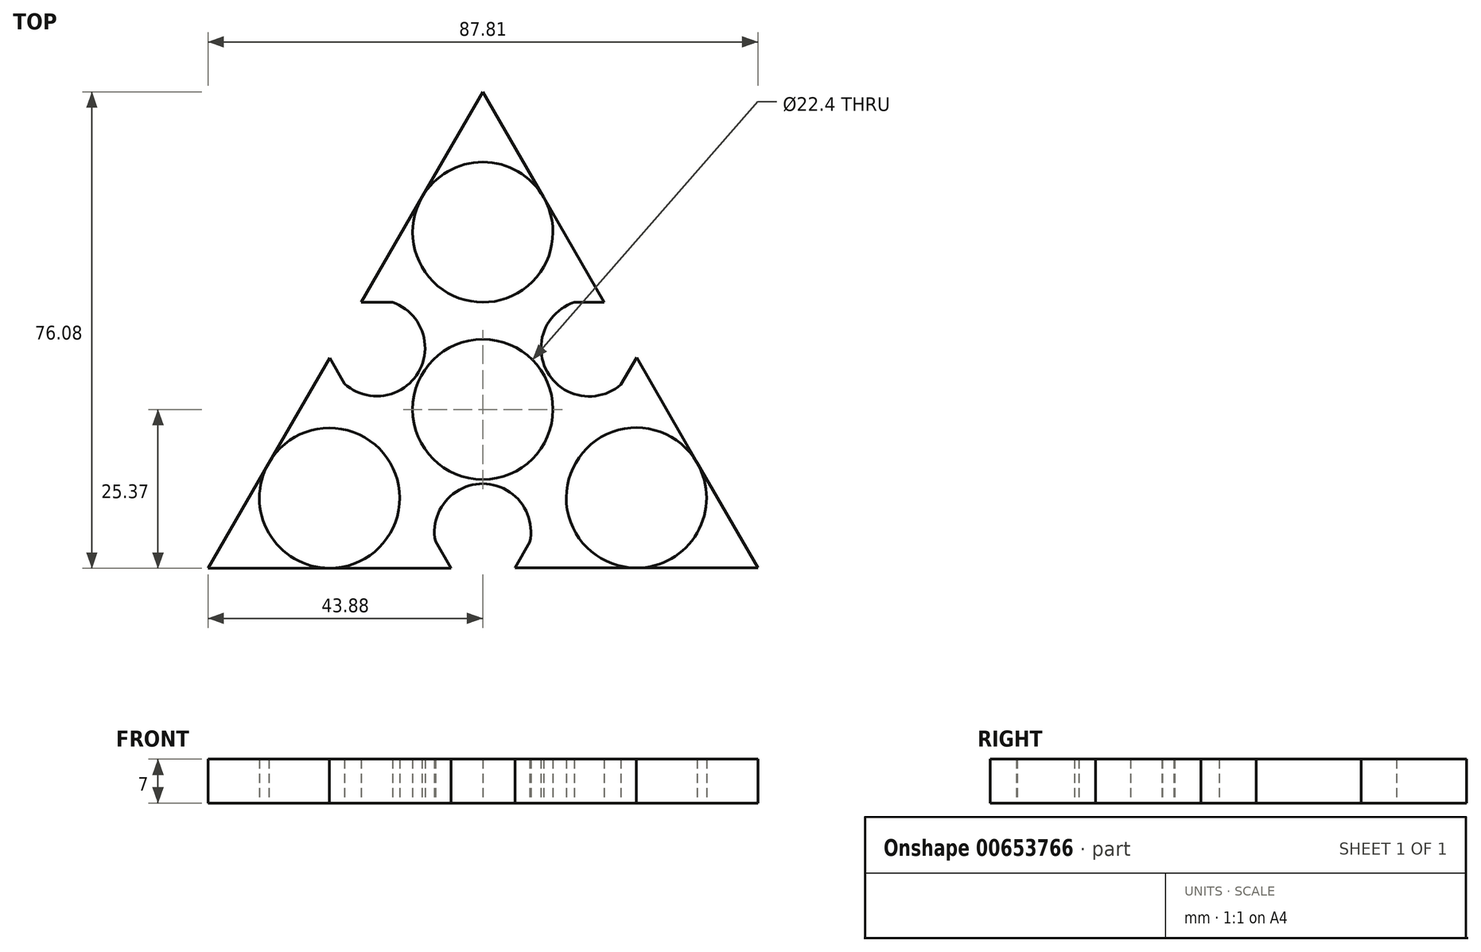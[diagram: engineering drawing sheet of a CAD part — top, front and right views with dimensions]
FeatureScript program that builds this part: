
annotation { "Feature Type Name" : "Feature", "Feature Type Description" : "" }
export const myFeature = defineFeature(function(context is Context, id is Id, definition is map)
    precondition{}
    {
        {
            var Q0;
            Q0=qCreatedBy(makeId("Top.planeOp"),FACE);
            var sketch = newSketch(context, id + "F0", { "sketchPlane" : qUnion([Q0])});
            skCircle(sketch, "E0", {"center": v(0, 0) * mm, "radius": 11.2 * mm});
            skCircle(sketch, "E1.cCircle", {"center": v(0, 28.3) * mm, "radius": 11.2 * mm, "construction": true});
            skLineSegment(sketch, "E1.0", {"start": v(-19.4, 17.12) * mm, "end": v(0.02, 50.7) * mm});
            skLineSegment(sketch, "E1.1", {"start": v(0.02, 50.7) * mm, "end": v(19.4, 17.1) * mm});
            skLineSegment(sketch, "E1.2", {"start": v(19.4, 17.1) * mm, "end": v(-19.4, 17.12) * mm});
            skPoint(sketch, "E1.0.midPoint", {"position": v(-9.7, 33.92) * mm});
            skCircle(sketch, "E2", {"center": v(0, 28.3) * mm, "radius": 11.2 * mm});
            skLineSegment(sketch, "E3.1.0", {"start": v(-43.88, -25.34) * mm, "end": v(-24.46, 8.25) * mm});
            skLineSegment(sketch, "E3.1.1", {"start": v(-5.08, -25.37) * mm, "end": v(-43.88, -25.34) * mm});
            skCircle(sketch, "E3.1.2", {"center": v(-24.47, -14.15) * mm, "radius": 11.2 * mm, "construction": true});
            skLineSegment(sketch, "E3.1.3", {"start": v(-24.46, 8.25) * mm, "end": v(-5.08, -25.37) * mm});
            skLineSegment(sketch, "E3.2.0", {"start": v(43.93, -25.33) * mm, "end": v(5.13, -25.3) * mm});
            skLineSegment(sketch, "E3.2.1", {"start": v(24.55, 8.28) * mm, "end": v(43.93, -25.33) * mm});
            skCircle(sketch, "E3.2.2", {"center": v(24.54, -14.12) * mm, "radius": 11.2 * mm, "construction": true});
            skLineSegment(sketch, "E3.2.3", {"start": v(5.13, -25.3) * mm, "end": v(24.55, 8.28) * mm});
            skPoint(sketch, "E3.center", {"position": v(0.02, 0.01) * mm});
            skCircle(sketch, "E4", {"center": v(24.54, -14.12) * mm, "radius": 11.2 * mm});
            skCircle(sketch, "E5", {"center": v(-24.47, -14.15) * mm, "radius": 11.2 * mm});
            skArc(sketch, "E6", {"start": v(19.4, 17.1) * mm, "mid": v(10.36, 5.88) * mm, "end": v(24.55, 8.28) * mm});
            skArc(sketch, "E7", {"start": v(5.13, -25.3) * mm, "mid": v(-0.07, -11.87) * mm, "end": v(-5.08, -25.37) * mm});
            skArc(sketch, "E8", {"start": v(-24.46, 8.25) * mm, "mid": v(-10.23, 6.03) * mm, "end": v(-19.4, 17.12) * mm});
            skSolve(sketch);
        }
        {
            var Q0;
            {var subQ0=sQuery(id+"F0.wireOp",EDGE,"E1.1");var subQ1=sQuery(id+"F0.wireOp",EDGE,"E1.0");var subQ2=makeQuery(id+"F0.imprint","INTERSECT",VERTEX,{"derivedFrom":[subQ1,subQ0]});Q0=makeQuery(id+"F0.imprint","IMPRINT",FACE,{"disambiguationData":[TD([[makeQuery(id+"F0.imprint","IMPRINT",EDGE,{"disambiguationData":[TD([[subQ2,1.0]])],"derivedFrom":subQ1}),-1.0]])]});}
            var Q1;
            {var subQ0=sQuery(id+"F0.wireOp",EDGE,"E6");var subQ1=sQuery(id+"F0.wireOp",EDGE,"E1.2");var subQ3=makeQuery(id+"F0.imprint","INTERSECT",VERTEX,{"derivedFrom":[subQ1,subQ0]});Q1=makeQuery(id+"F0.imprint","IMPRINT",FACE,{"disambiguationData":[TD([[makeQuery(id+"F0.imprint","IMPRINT",EDGE,{"disambiguationData":[TD([[subQ3,1.0]])],"derivedFrom":subQ1}),-1.0]])]});}
            var Q2;
            {var subQ0=sQuery(id+"F0.wireOp",EDGE,"E8");var subQ1=sQuery(id+"F0.wireOp",EDGE,"E1.2");var subQ3=makeQuery(id+"F0.imprint","INTERSECT",VERTEX,{"derivedFrom":[subQ1,subQ0]});Q2=makeQuery(id+"F0.imprint","IMPRINT",FACE,{"disambiguationData":[TD([[makeQuery(id+"F0.imprint","IMPRINT",EDGE,{"disambiguationData":[TD([[subQ3,-1.0]])],"derivedFrom":subQ1}),-1.0]])]});}
            var Q3;
            {var subQ0=sQuery(id+"F0.wireOp",EDGE,"E3.1.1");var subQ1=sQuery(id+"F0.wireOp",EDGE,"E3.1.0");var subQ2=makeQuery(id+"F0.imprint","INTERSECT",VERTEX,{"derivedFrom":[subQ1,subQ0]});Q3=makeQuery(id+"F0.imprint","IMPRINT",FACE,{"disambiguationData":[TD([[makeQuery(id+"F0.imprint","IMPRINT",EDGE,{"disambiguationData":[TD([[subQ2,-1.0]])],"derivedFrom":subQ1}),-1.0]])]});}
            var Q4;
            {var subQ0=sQuery(id+"F0.wireOp",EDGE,"E8");var subQ1=sQuery(id+"F0.wireOp",EDGE,"E3.1.3");var subQ3=makeQuery(id+"F0.imprint","INTERSECT",VERTEX,{"derivedFrom":[subQ1,subQ0]});Q4=makeQuery(id+"F0.imprint","IMPRINT",FACE,{"disambiguationData":[TD([[makeQuery(id+"F0.imprint","IMPRINT",EDGE,{"disambiguationData":[TD([[subQ3,1.0]])],"derivedFrom":subQ1}),-1.0]])]});}
            var Q5;
            {var subQ0=sQuery(id+"F0.wireOp",EDGE,"E7");var subQ1=sQuery(id+"F0.wireOp",EDGE,"E3.1.3");var subQ3=makeQuery(id+"F0.imprint","INTERSECT",VERTEX,{"derivedFrom":[subQ1,subQ0]});Q5=makeQuery(id+"F0.imprint","IMPRINT",FACE,{"disambiguationData":[TD([[makeQuery(id+"F0.imprint","IMPRINT",EDGE,{"disambiguationData":[TD([[subQ3,-1.0]])],"derivedFrom":subQ1}),-1.0]])]});}
            var Q6;
            {var subQ0=sQuery(id+"F0.wireOp",EDGE,"E3.2.1");var subQ1=sQuery(id+"F0.wireOp",EDGE,"E3.2.0");var subQ2=makeQuery(id+"F0.imprint","INTERSECT",VERTEX,{"derivedFrom":[subQ1,subQ0]});Q6=makeQuery(id+"F0.imprint","IMPRINT",FACE,{"disambiguationData":[TD([[makeQuery(id+"F0.imprint","IMPRINT",EDGE,{"disambiguationData":[TD([[subQ2,-1.0]])],"derivedFrom":subQ1}),-1.0]])]});}
            var Q7;
            {var subQ0=sQuery(id+"F0.wireOp",EDGE,"E7");var subQ1=sQuery(id+"F0.wireOp",EDGE,"E3.2.3");var subQ3=makeQuery(id+"F0.imprint","INTERSECT",VERTEX,{"derivedFrom":[subQ1,subQ0]});Q7=makeQuery(id+"F0.imprint","IMPRINT",FACE,{"disambiguationData":[TD([[makeQuery(id+"F0.imprint","IMPRINT",EDGE,{"disambiguationData":[TD([[subQ3,1.0]])],"derivedFrom":subQ1}),-1.0]])]});}
            var Q8;
            {var subQ0=sQuery(id+"F0.wireOp",EDGE,"E6");var subQ1=sQuery(id+"F0.wireOp",EDGE,"E3.2.3");var subQ3=makeQuery(id+"F0.imprint","INTERSECT",VERTEX,{"derivedFrom":[subQ1,subQ0]});Q8=makeQuery(id+"F0.imprint","IMPRINT",FACE,{"disambiguationData":[TD([[makeQuery(id+"F0.imprint","IMPRINT",EDGE,{"disambiguationData":[TD([[subQ3,-1.0]])],"derivedFrom":subQ1}),-1.0]])]});}
            var Q9;
            {var subQ0=sQuery(id+"F0.wireOp",EDGE,"E8");var subQ1=sQuery(id+"F0.wireOp",EDGE,"E1.2");var subQ6=makeQuery(id+"F0.imprint","INTERSECT",VERTEX,{"derivedFrom":[subQ1,subQ0]});Q9=makeQuery(id+"F0.imprint","IMPRINT",FACE,{"disambiguationData":[TD([[makeQuery(id+"F0.imprint","IMPRINT",EDGE,{"disambiguationData":[TD([[subQ6,1.0]])],"derivedFrom":subQ1}),-1.0]])]});}
            var Q10;
            {var subQ0=sQuery(id+"F0.wireOp",EDGE,"E6");var subQ1=sQuery(id+"F0.wireOp",EDGE,"E1.2");var subQ6=makeQuery(id+"F0.imprint","INTERSECT",VERTEX,{"derivedFrom":[subQ1,subQ0]});Q10=makeQuery(id+"F0.imprint","IMPRINT",FACE,{"disambiguationData":[TD([[makeQuery(id+"F0.imprint","IMPRINT",EDGE,{"disambiguationData":[TD([[subQ6,-1.0]])],"derivedFrom":subQ1}),-1.0]])]});}
            var Q11;
            {var subQ0=sQuery(id+"F0.wireOp",EDGE,"E8");var subQ1=sQuery(id+"F0.wireOp",EDGE,"E3.1.3");var subQ6=makeQuery(id+"F0.imprint","INTERSECT",VERTEX,{"derivedFrom":[subQ1,subQ0]});Q11=makeQuery(id+"F0.imprint","IMPRINT",FACE,{"disambiguationData":[TD([[makeQuery(id+"F0.imprint","IMPRINT",EDGE,{"disambiguationData":[TD([[subQ6,-1.0]])],"derivedFrom":subQ1}),-1.0]])]});}
            var Q12;
            {var subQ0=sQuery(id+"F0.wireOp",EDGE,"E7");var subQ1=sQuery(id+"F0.wireOp",EDGE,"E3.1.3");var subQ6=makeQuery(id+"F0.imprint","INTERSECT",VERTEX,{"derivedFrom":[subQ1,subQ0]});Q12=makeQuery(id+"F0.imprint","IMPRINT",FACE,{"disambiguationData":[TD([[makeQuery(id+"F0.imprint","IMPRINT",EDGE,{"disambiguationData":[TD([[subQ6,1.0]])],"derivedFrom":subQ1}),-1.0]])]});}
            var Q13;
            {var subQ0=sQuery(id+"F0.wireOp",EDGE,"E7");var subQ1=sQuery(id+"F0.wireOp",EDGE,"E3.2.3");var subQ6=makeQuery(id+"F0.imprint","INTERSECT",VERTEX,{"derivedFrom":[subQ1,subQ0]});Q13=makeQuery(id+"F0.imprint","IMPRINT",FACE,{"disambiguationData":[TD([[makeQuery(id+"F0.imprint","IMPRINT",EDGE,{"disambiguationData":[TD([[subQ6,-1.0]])],"derivedFrom":subQ1}),-1.0]])]});}
            var Q14;
            {var subQ0=sQuery(id+"F0.wireOp",EDGE,"E6");var subQ1=sQuery(id+"F0.wireOp",EDGE,"E3.2.3");var subQ6=makeQuery(id+"F0.imprint","INTERSECT",VERTEX,{"derivedFrom":[subQ1,subQ0]});Q14=makeQuery(id+"F0.imprint","IMPRINT",FACE,{"disambiguationData":[TD([[makeQuery(id+"F0.imprint","IMPRINT",EDGE,{"disambiguationData":[TD([[subQ6,1.0]])],"derivedFrom":subQ1}),-1.0]])]});}
            var Q15;
            Q15=makeQuery(id+"F0.imprint","IMPRINT",FACE,{"disambiguationData":[TD([[makeQuery(id+"F0.imprint","IMPRINT",EDGE,{"derivedFrom":sQuery(id+"F0.wireOp",EDGE,"E0")}),-1.0]])]});
            extrude(context, id + "F1", {"entities" : qUnion([Q0, Q1, Q2, Q3, Q4, Q5, Q6, Q7, Q8, Q9, Q10, Q11, Q12, Q13, Q14, Q15]), "depth" : 7 * mm, "offsetDistance" : 25 * mm});
        }
    });
